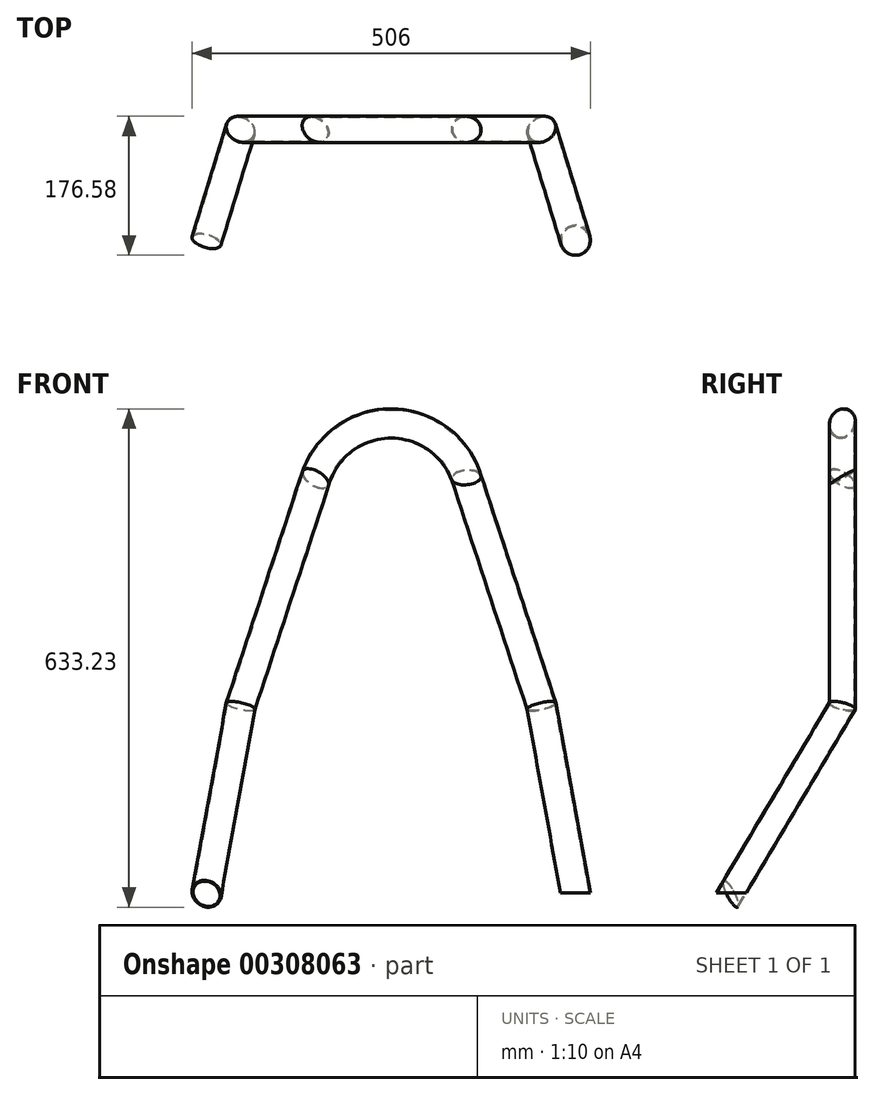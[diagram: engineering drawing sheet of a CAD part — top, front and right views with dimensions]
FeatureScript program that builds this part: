
annotation { "Feature Type Name" : "Feature", "Feature Type Description" : "" }
export const myFeature = defineFeature(function(context is Context, id is Id, definition is map)
    precondition{}
    {
        {
            var Q0;
            Q0=qCreatedBy(makeId("Front.planeOp"),FACE);
            var sketch = newSketch(context, id + "F0", { "sketchPlane" : qUnion([Q0])});
            skLineSegment(sketch, "E0", {"start": v(-76.3, 0) * mm, "end": v(76.23, 0) * mm});
            skLineSegment(sketch, "E1", {"start": v(0, 0) * mm, "end": v(0, 355.6) * mm});
            skArc(sketch, "E2", {"start": v(96.51, 285.74) * mm, "mid": v(59.57, 336.3) * mm, "end": v(0, 355.6) * mm});
            skLineSegment(sketch, "E3", {"start": v(191.75, -3.8) * mm, "end": v(96.51, 285.74) * mm});
            skLineSegment(sketch, "E4.0", {"start": v(-234.95, -241.3) * mm, "end": v(234.95, -241.3) * mm});
            skLineSegment(sketch, "E5", {"start": v(0, 0) * mm, "end": v(0, -241.3) * mm});
            skLineSegment(sketch, "E6.0", {"start": v(234.95, 0) * mm, "end": v(234.95, -241.3) * mm});
            skLineSegment(sketch, "E7.0", {"start": v(-234.95, 0) * mm, "end": v(-234.95, -241.3) * mm});
            skArc(sketch, "E8.MirrorCS", {"start": v(-96.51, 285.74) * mm, "mid": v(-59.57, 336.3) * mm, "end": v(0, 355.6) * mm});
            skLineSegment(sketch, "E9.MirrorCS", {"start": v(-191.75, -3.8) * mm, "end": v(-96.51, 285.74) * mm});
            skSolve(sketch);
        }
        {
            var Q0;
            Q0=qCreatedBy(makeId("Right.planeOp"),FACE);
            cPlane(context, id + "F1", {"entities" : qUnion([Q0]), "cplaneType" : CPlaneType.OFFSET, "offset" : 234.95 * mm, "width" : 152.4 * mm, "height" : 152.4 * mm});
        }
        {
            var Q0;
            Q0=qCreatedBy(id+"F1.planeOp",FACE);
            var sketch = newSketch(context, id + "F2", { "sketchPlane" : qUnion([Q0])});
            skLineSegment(sketch, "E10", {"start": v(0, 0) * mm, "end": v(-141.2, -241.29) * mm});
            skLineSegment(sketch, "E11", {"start": v(0, -241.29) * mm, "end": v(-141.2, -241.29) * mm});
            skSolve(sketch);
        }
        {
            var Q0;
            Q0=sQuery(id+"F2.wireOp",VERTEX,"E10.end");
            var Q1;
            Q1=sQuery(id+"F2.wireOp",VERTEX,"E11.start");
            var Q2;
            Q2=sQuery(id+"F0.wireOp",VERTEX,"E3.start");
            cPlane(context, id + "F3", {"entities" : qUnion([Q0, Q1, Q2]), "cplaneType" : CPlaneType.THREE_POINT, "offset" : 0 * mm, "width" : 152.4 * mm, "height" : 152.4 * mm});
        }
        {
            var Q0;
            Q0=qCreatedBy(id+"F3.planeOp",FACE);
            var sketch = newSketch(context, id + "F4", { "sketchPlane" : qUnion([Q0])});
            skLineSegment(sketch, "E12", {"start": v(0, -38.05) * mm, "end": v(141.2, -279.44) * mm});
            skLineSegment(sketch, "E13.MirrorCS", {"start": v(0, 2104.73) * mm, "end": v(141.2, 2346.12) * mm});
            skSolve(sketch);
        }
        {
            var Q0;
            Q0=qCreatedBy(makeId("Top.planeOp"),FACE);
            cPlane(context, id + "F5", {"entities" : qUnion([Q0]), "cplaneType" : CPlaneType.OFFSET, "offset" : 241.3 * mm, "oppositeDirection" : true, "width" : 152.4 * mm, "height" : 152.4 * mm});
        }
        {
            var Q0;
            Q0=qCreatedBy(id+"F5.planeOp",FACE);
            var sketch = newSketch(context, id + "F6", { "sketchPlane" : qUnion([Q0])});
            skCircle(sketch, "E14", {"center": v(234.16, -139.84) * mm, "radius": 19.05 * mm});
            skCircle(sketch, "E15", {"center": v(234.16, -139.84) * mm, "radius": 17.78 * mm});
            skSolve(sketch);
        }
        {
            var Q0;
            Q0=sQuery(id+"F0.wireOp",EDGE,"E7.0");
            cPlane(context, id + "F7", {"entities" : qUnion([Q0]), "cplaneType" : CPlaneType.LINE_ANGLE, "offset" : 25.4 * mm, "angle" : 0 * degree, "width" : 152.4 * mm, "height" : 152.4 * mm});
        }
        {
            var Q0;
            Q0=qCreatedBy(id+"F7.planeOp",FACE);
            var sketch = newSketch(context, id + "F8", { "sketchPlane" : qUnion([Q0])});
            skLineSegment(sketch, "E16.0", {"start": v(0, 0) * mm, "end": v(0, -241.3) * mm});
            skLineSegment(sketch, "E16.1", {"start": v(0, 0) * mm, "end": v(141.2, -241.29) * mm});
            skLineSegment(sketch, "E16.2", {"start": v(0, -241.29) * mm, "end": v(141.2, -241.29) * mm});
            skSolve(sketch);
        }
        {
            var Q0;
            Q0=sQuery(id+"F0.wireOp",VERTEX,"E9.MirrorCS.start");
            var Q1;
            Q1=sQuery(id+"F0.wireOp",VERTEX,"E4.0.start");
            var Q2;
            Q2=sQuery(id+"F8.wireOp",VERTEX,"E16.1.end");
            cPlane(context, id + "F9", {"entities" : qUnion([Q0, Q1, Q2]), "cplaneType" : CPlaneType.THREE_POINT, "offset" : 25.4 * mm, "width" : 152.4 * mm, "height" : 152.4 * mm});
        }
        {
            var Q0;
            Q0=qCreatedBy(id+"F9.planeOp",FACE);
            var sketch = newSketch(context, id + "F10", { "sketchPlane" : qUnion([Q0])});
            skPoint(sketch, "E17.1", {"position": v(-70.6, -160.74) * mm});
            skPoint(sketch, "E18.0", {"position": v(0, -38.05) * mm});
            skLineSegment(sketch, "E19", {"start": v(0, -38.05) * mm, "end": v(-141.21, -279.44) * mm});
            skSolve(sketch);
        }
        {
            var Q0;
            Q0=makeQuery(id+"F6.imprint","IMPRINT",FACE,{"disambiguationData":[TD([[makeQuery(id+"F6.imprint","IMPRINT",EDGE,{"derivedFrom":sQuery(id+"F6.wireOp",EDGE,"E14")}),1.0]])]});
            var Q1;
            Q1=sQuery(id+"F4.wireOp",EDGE,"E12");
            var Q2;
            Q2=sQuery(id+"F0.wireOp",EDGE,"E3");
            var Q3;
            Q3=sQuery(id+"F0.wireOp",EDGE,"E2");
            var Q4;
            Q4=sQuery(id+"F0.wireOp",EDGE,"E8.MirrorCS");
            var Q5;
            Q5=sQuery(id+"F0.wireOp",EDGE,"E9.MirrorCS");
            var Q6;
            Q6=sQuery(id+"F10.wireOp",EDGE,"E19");
            sweep(context, id + "F11", {"profiles" : qUnion([Q0]), "path" : qUnion([Q1, Q2, Q3, Q4, Q5, Q6])});
        }
    });
